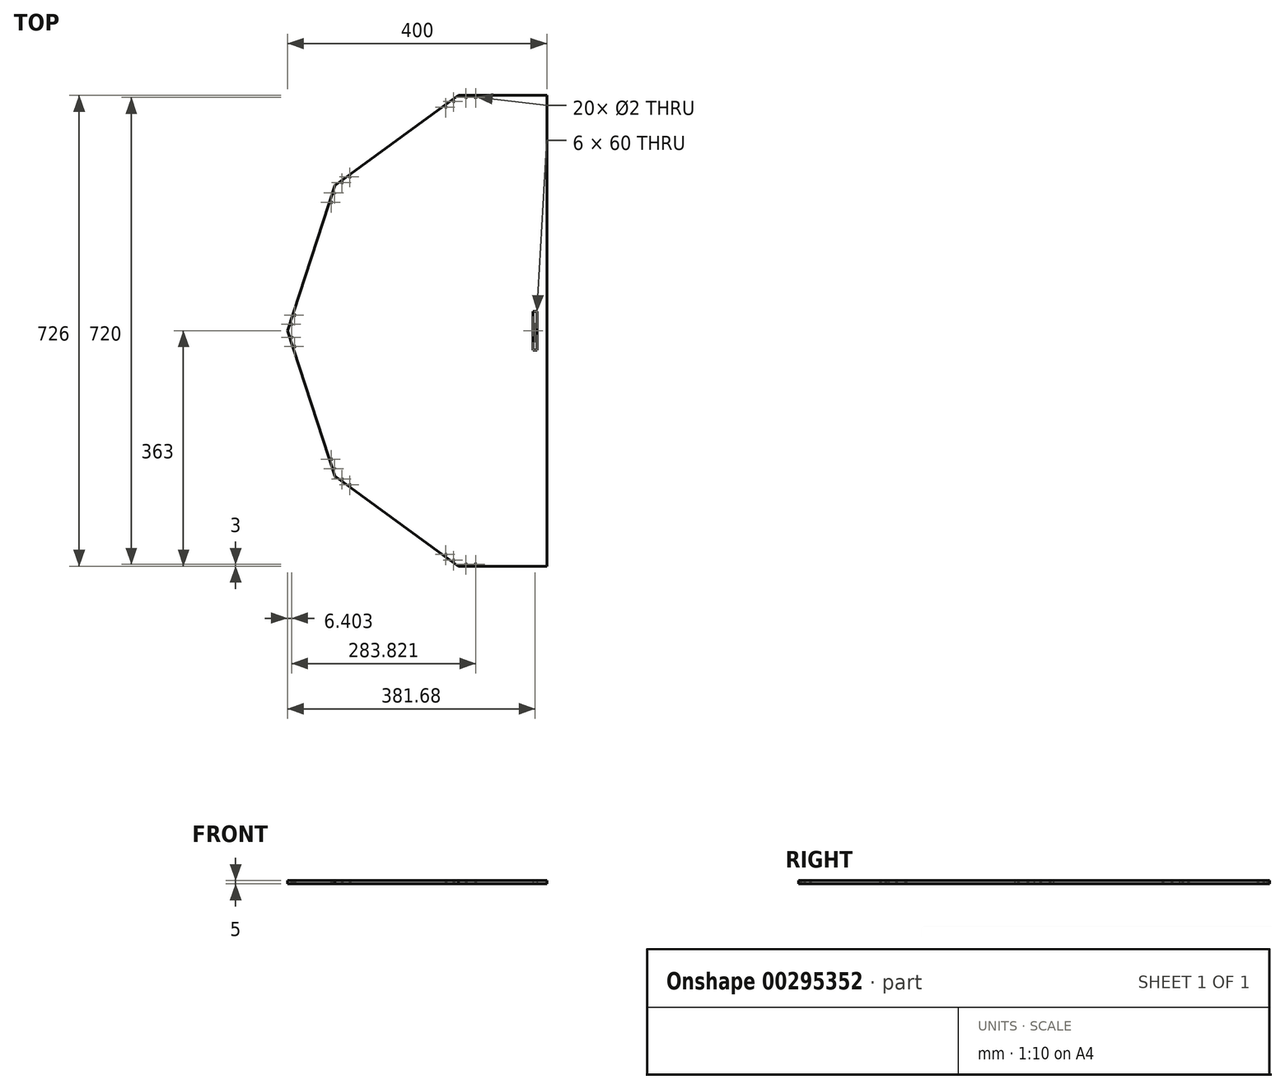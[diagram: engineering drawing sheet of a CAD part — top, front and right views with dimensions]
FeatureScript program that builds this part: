
annotation { "Feature Type Name" : "Feature", "Feature Type Description" : "" }
export const myFeature = defineFeature(function(context is Context, id is Id, definition is map)
    precondition{}
    {
        {
            var Q0;
            Q0=qCreatedBy(makeId("Top.planeOp"),FACE);
            var sketch = newSketch(context, id + "F0", { "sketchPlane" : qUnion([Q0])});
            skLineSegment(sketch, "E0.2", {"start": v(18.32, -363) * mm, "end": v(-117.95, -363) * mm});
            skLineSegment(sketch, "E0.3", {"start": v(-117.95, -363) * mm, "end": v(-308.79, -224.35) * mm});
            skLineSegment(sketch, "E0.4", {"start": v(-308.79, -224.35) * mm, "end": v(-381.68, 0) * mm});
            skLineSegment(sketch, "E0.5", {"start": v(-381.68, 0) * mm, "end": v(-308.79, 224.35) * mm});
            skLineSegment(sketch, "E0.6", {"start": v(-308.79, 224.35) * mm, "end": v(-117.95, 363) * mm});
            skLineSegment(sketch, "E0.7", {"start": v(-117.95, 363) * mm, "end": v(18.32, 363) * mm});
            skCircle(sketch, "E1.3.1", {"center": v(-125.48, 353.82) * mm, "radius": 1 * mm});
            skCircle(sketch, "E1.3.3", {"center": v(-137.61, 345) * mm, "radius": 1 * mm});
            skCircle(sketch, "E1.4.1", {"center": v(-309.48, 212.5) * mm, "radius": 1 * mm});
            skCircle(sketch, "E1.4.3", {"center": v(-314.12, 198.23) * mm, "radius": 1 * mm});
            skCircle(sketch, "E1.5.1", {"center": v(-375.28, -10) * mm, "radius": 1 * mm});
            skCircle(sketch, "E1.5.3", {"center": v(-370.64, -24.27) * mm, "radius": 1 * mm});
            skCircle(sketch, "E1.6.1", {"center": v(-297.73, -228.67) * mm, "radius": 1 * mm});
            skCircle(sketch, "E1.6.3", {"center": v(-285.6, -237.49) * mm, "radius": 1 * mm});
            skCircle(sketch, "E1.7.1", {"center": v(-106.46, -360) * mm, "radius": 1 * mm});
            skCircle(sketch, "E1.7.3", {"center": v(-91.46, -360) * mm, "radius": 1 * mm});
            skLineSegment(sketch, "E2.trimOffspring", {"start": v(18.32, 363) * mm, "end": v(18.32, -363) * mm});
            skLineSegment(sketch, "E3.bottom", {"start": v(3, -30) * mm, "end": v(-3, -30) * mm});
            skLineSegment(sketch, "E3.top", {"start": v(3, 30) * mm, "end": v(-3, 30) * mm});
            skLineSegment(sketch, "E3.left", {"start": v(3, -30) * mm, "end": v(3, 30) * mm});
            skLineSegment(sketch, "E3.right", {"start": v(-3, -30) * mm, "end": v(-3, 30) * mm});
            skPoint(sketch, "E3.middle", {"position": v(0, 0) * mm});
            skCircle(sketch, "E4", {"center": v(-106.46, 360) * mm, "radius": 1 * mm});
            skCircle(sketch, "E5", {"center": v(-91.46, 360) * mm, "radius": 1 * mm});
            skCircle(sketch, "E6", {"center": v(-297.73, 228.67) * mm, "radius": 1 * mm});
            skCircle(sketch, "E7", {"center": v(-285.6, 237.49) * mm, "radius": 1 * mm});
            skCircle(sketch, "E8", {"center": v(-375.28, 10) * mm, "radius": 1 * mm});
            skCircle(sketch, "E9", {"center": v(-370.64, 24.27) * mm, "radius": 1 * mm});
            skCircle(sketch, "E10", {"center": v(-314.12, -198.23) * mm, "radius": 1 * mm});
            skCircle(sketch, "E11", {"center": v(-309.48, -212.5) * mm, "radius": 1 * mm});
            skCircle(sketch, "E12", {"center": v(-125.48, -353.82) * mm, "radius": 1 * mm});
            skCircle(sketch, "E13", {"center": v(-137.61, -345) * mm, "radius": 1 * mm});
            skSolve(sketch);
        }
        {
            var Q0;
            Q0=makeQuery(id+"F0.imprint","IMPRINT",FACE,{"disambiguationData":[TD([[makeQuery(id+"F0.imprint","IMPRINT",EDGE,{"derivedFrom":sQuery(id+"F0.wireOp",EDGE,"E0.2")}),-1.0]])]});
            extrude(context, id + "F1", {"entities" : qUnion([Q0]), "depth" : 5 * mm});
        }
    });
